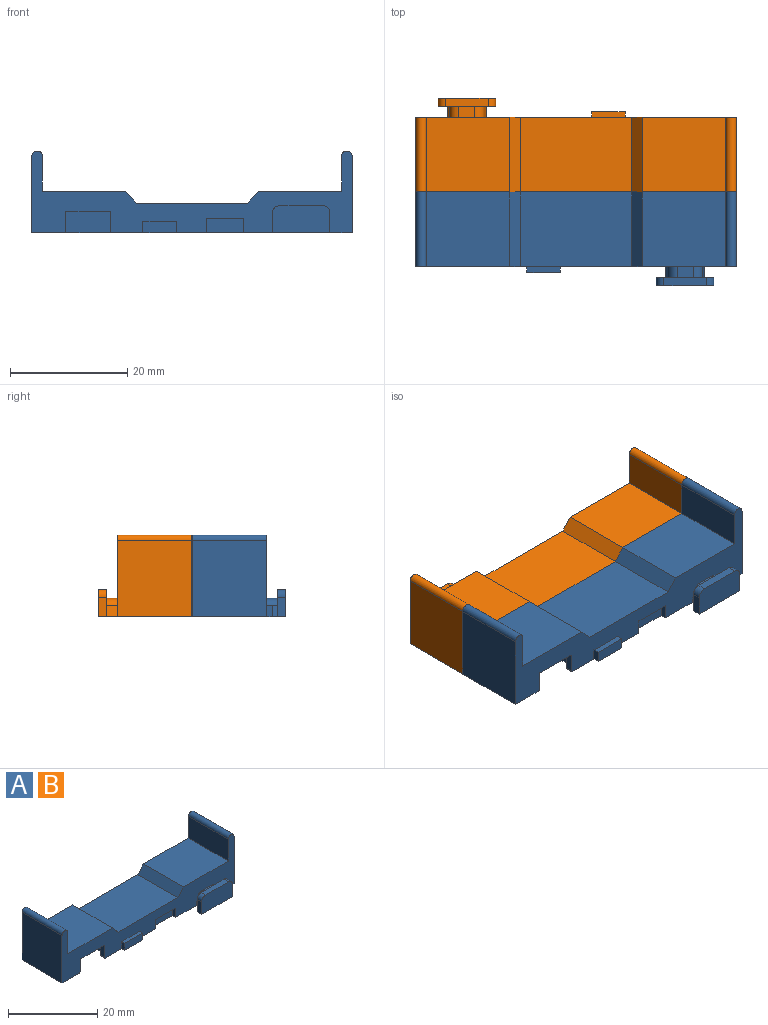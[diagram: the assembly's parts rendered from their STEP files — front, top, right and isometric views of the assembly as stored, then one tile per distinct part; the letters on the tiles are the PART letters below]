
ASSEMBLY  parts=2 mates=1
PART A: 46 faces, bbox 54.6x16x14 mm
  f0: plane 54.61x13.97mm, normal (0,-1,0), area 296.6mm2, adj f1,f2,f3,f4,f5,f6,f7,f8
  f1: plane 19x12.7mm, normal (0,0,1), area 241.3mm2, adj f0,f2,f12,f13
  f2: plane 12.7x2.03mm, normal (0.75,0,0.66), area 34.3mm2, adj f0,f1,f3,f13
  f3: plane 14.22x12.7mm, normal (0,0,1), area 180.6mm2, adj f0,f2,f4,f13
  f4: plane 12.7x5.96mm, normal (1,0,0), area 75.6mm2, adj f0,f3,f5,f13
  f5: cylinder r=0.9mm len=12.7mm, axis (0,-1,0), area 36mm2, adj f0,f4,f6,f13
  f6: plane 13.07x12.7mm, normal (-1,0,0), area 166mm2, adj f0,f5,f7,f13
  f7: plane 54.61x16mm, normal (0,0,-1), area 671.6mm2, adj f0,f6,f8,f13,f17,f18,f19,f21
  f8: plane 13.07x12.7mm, normal (1,0,0), area 166mm2, adj f0,f7,f9,f13
  f9: cylinder r=0.9mm len=12.7mm, axis (0,-1,0), area 36mm2, adj f0,f8,f10,f13
  f10: plane 12.7x5.96mm, normal (-1,0,0), area 75.6mm2, adj f0,f9,f11,f13
  f11: plane 14.22x12.7mm, normal (0,0,1), area 180.6mm2, adj f0,f10,f12,f13
  f12: plane 12.7x2.03mm, normal (-0.75,0,0.66), area 34.3mm2, adj f0,f1,f11,f13
  f13: plane 54.61x13.97mm, normal (0,1,0), area 370.2mm2, adj f1,f2,f3,f4,f5,f6,f7,f8
  f14: plane 3.15x1.27mm, normal (1,0,0), area 4mm2, adj f0,f17,f23,f24
  f15: plane 3.15x1.27mm, normal (-1,0,0), area 4mm2, adj f0,f17,f22,f25
  f16: plane 7.24x1.27mm, normal (0,0,-1), area 9.2mm2, adj f0,f17,f22,f23
  f17: plane 10.36x5.61mm, normal (0,1,0), area 29.8mm2, adj f7,f14,f15,f16,f18,f19,f20,f22
  f18: plane 5.61x3.58mm, normal (1,0,0), area 20.1mm2, adj f7,f17,f20,f21
  f19: plane 5.61x3.58mm, normal (-1,0,0), area 20.1mm2, adj f7,f17,f20,f21
  f20: plane 10.36x3.58mm, normal (0,0,-1), area 37.1mm2, adj f17,f18,f19,f21
  f21: plane 10.36x5.61mm, normal (0,-1,0), area 58.2mm2, adj f7,f18,f19,f20
  f22: cylinder r=0.25mm len=1.27mm, axis (0,-1,0), area 0.5mm2, adj f0,f15,f16,f17
  f23: cylinder r=0.25mm len=1.27mm, axis (0,1,0), area 0.5mm2, adj f0,f14,f16,f17
  f24: cylinder r=0.25mm len=1.27mm, axis (0,1,0), area 0.5mm2, adj f0,f7,f14,f17
  f25: cylinder r=0.25mm len=1.27mm, axis (0,-1,0), area 0.5mm2, adj f0,f7,f15,f17
  f26: plane 1.91x1.89mm, normal (-0.98,0,0.2), area 3.7mm2, adj f0,f7,f30,f31
  f27: plane 1.91x1.89mm, normal (0.98,0,0.2), area 3.7mm2, adj f0,f7,f28,f31
  f28: cylinder r=1.6mm len=1.91mm, axis (0,1,0), area 4.2mm2, adj f0,f27,f29,f31
  f29: plane 2.71x1.91mm, normal (0,0,1), area 5.2mm2, adj f0,f28,f30,f31
  f30: cylinder r=1.6mm len=1.91mm, axis (0,1,0), area 4.2mm2, adj f0,f26,f29,f31
  f31: plane 9.8x4.67mm, normal (0,1,0), area 26.9mm2, adj f7,f26,f27,f28,f29,f30,f32,f33
  f32: plane 3.4x1.4mm, normal (1,0,0), area 4.8mm2, adj f7,f31,f33,f37
  f33: cylinder r=1.27mm len=1.4mm, axis (0,1,0), area 2.8mm2, adj f31,f32,f34,f37
  f34: plane 7.26x1.4mm, normal (0,0,1), area 10.1mm2, adj f31,f33,f35,f37
  f35: cylinder r=1.27mm len=1.4mm, axis (0,1,0), area 2.8mm2, adj f31,f34,f36,f37
  f36: plane 3.4x1.4mm, normal (-1,0,0), area 4.8mm2, adj f7,f31,f35,f37
  f37: plane 9.8x4.67mm, normal (0,-1,0), area 45.1mm2, adj f7,f32,f33,f34,f35,f36
  f38: plane 1.91x1.02mm, normal (-1,0,0), area 1.9mm2, adj f0,f7,f40,f41
  f39: plane 1.91x1.02mm, normal (1,0,0), area 1.9mm2, adj f0,f7,f40,f41
  f40: plane 5.72x1.02mm, normal (0,0,1), area 5.8mm2, adj f0,f38,f39,f41
  f41: plane 5.72x1.91mm, normal (0,-1,0), area 10.9mm2, adj f7,f38,f39,f40
  f42: plane 2.54x1.02mm, normal (1,0,0), area 2.6mm2, adj f0,f7,f44,f45
  f43: plane 2.54x1.02mm, normal (-1,0,0), area 2.6mm2, adj f0,f7,f44,f45
  f44: plane 6.35x1.02mm, normal (0,0,-1), area 6.5mm2, adj f0,f42,f43,f45
  f45: plane 6.35x2.54mm, normal (0,-1,0), area 16.1mm2, adj f7,f42,f43,f44
PART B: same geometry as A
PLACE A at identity fixed
PLACE B rot(axis=(0,0,1),180deg) t=(0,25.4,0)mm
MATE planar B.f13 <-> A.f13  axis (0,-1,0) through (0,12.7,3.71)mm
